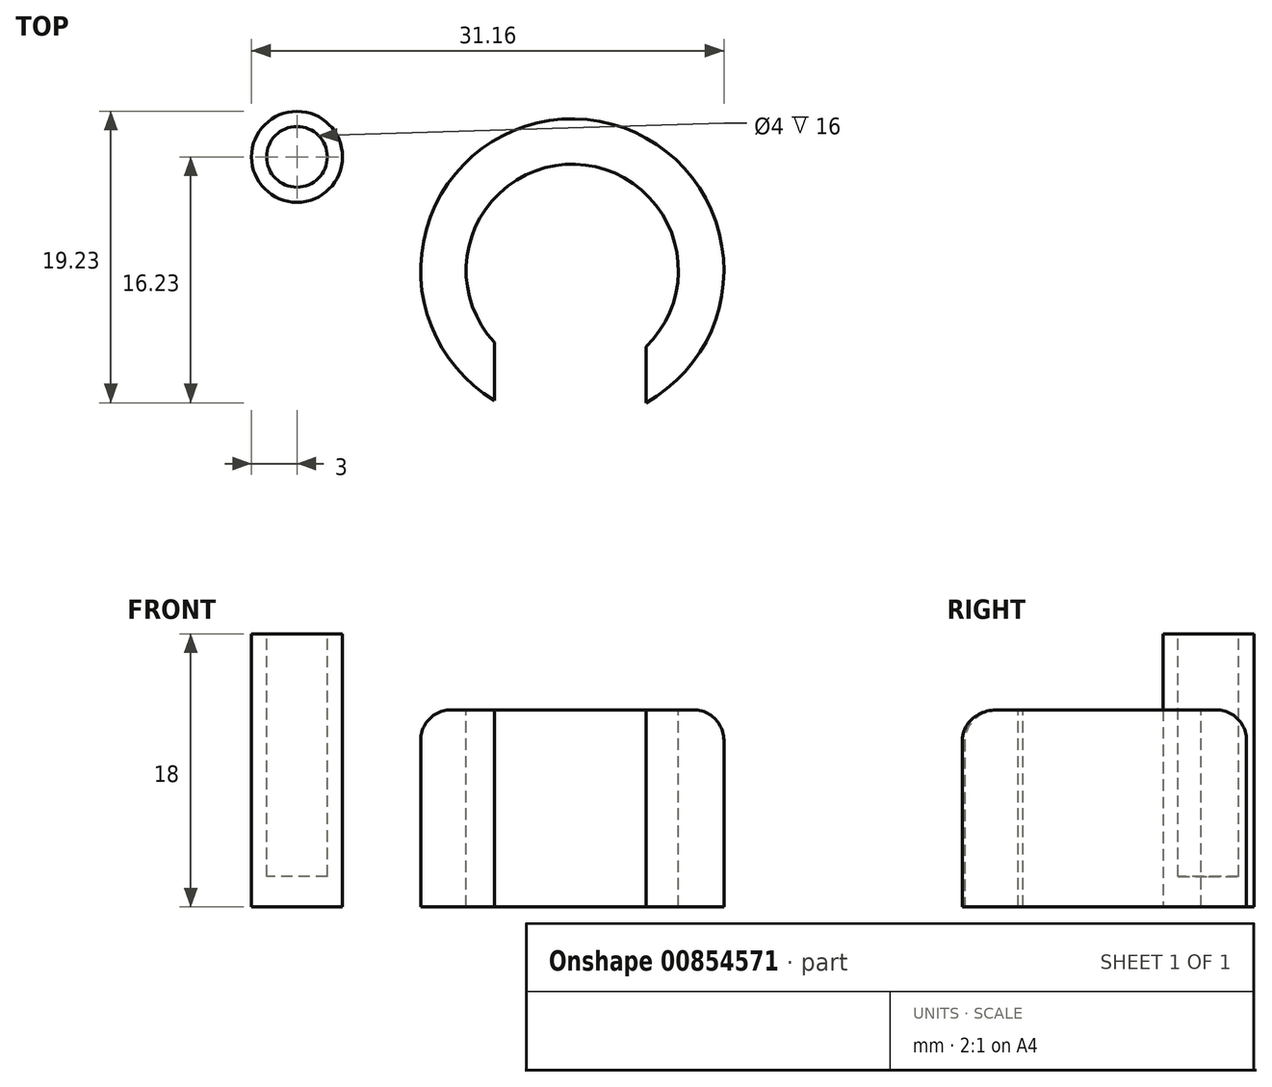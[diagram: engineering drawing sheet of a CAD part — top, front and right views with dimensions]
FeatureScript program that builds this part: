
annotation { "Feature Type Name" : "Feature", "Feature Type Description" : "" }
export const myFeature = defineFeature(function(context is Context, id is Id, definition is map)
    precondition{}
    {
        {
            var Q0;
            Q0=qCreatedBy(makeId("Top.planeOp"),FACE);
            var sketch = newSketch(context, id + "F0", { "sketchPlane" : qUnion([Q0])});
            skCircle(sketch, "E0", {"center": v(0, 0) * mm, "radius": 10 * mm});
            skSolve(sketch);
        }
        {
            var Q0;
            Q0 = qSketchRegion(id + "F0", true);
            extrude(context, id + "F1", {"entities" : qUnion([Q0]), "depth" : 13 * mm, "offsetDistance" : 25 * mm});
        }
        {
            var Q0;
            Q0=makeQuery(id+"F1.opExtrude","CAP_FACE",FACE,{"disambiguationData":[OSD([sQuery(id+"F0.wireOp",EDGE,"E0")])],"isStart":false});
            var sketch = newSketch(context, id + "F2", { "sketchPlane" : qUnion([Q0])});
            skCircle(sketch, "E1", {"center": v(0, 0) * mm, "radius": 7 * mm});
            skSolve(sketch);
        }
        {
            var Q0;
            Q0 = qSketchRegion(id + "F2", true);
            extrude(context, id + "F3", {"entities" : qUnion([Q0]), "operationType" : NewBodyOperationType.REMOVE, "oppositeDirection" : true, "depth" : 13 * mm, "offsetDistance" : 25 * mm});
        }
        {
            var Q0;
            Q0=makeQuery(id+"F1.opExtrude","CAP_FACE",FACE,{"disambiguationData":[OSD([sQuery(id+"F0.wireOp",EDGE,"E0")])],"isStart":false});
            var sketch = newSketch(context, id + "F4", { "sketchPlane" : qUnion([Q0])});
            skPoint(sketch, "E2.middle", {"position": v(0, 0) * mm});
            skLineSegment(sketch, "E3.bottom", {"start": v(-5.14, -2.24) * mm, "end": v(4.86, -2.24) * mm});
            skLineSegment(sketch, "E3.top", {"start": v(-5.14, -15.24) * mm, "end": v(4.86, -15.24) * mm});
            skLineSegment(sketch, "E3.left", {"start": v(-5.14, -2.24) * mm, "end": v(-5.14, -15.24) * mm});
            skLineSegment(sketch, "E3.right", {"start": v(4.86, -2.24) * mm, "end": v(4.86, -15.24) * mm});
            skSolve(sketch);
        }
        {
            var Q0;
            Q0 = qSketchRegion(id + "F4", true);
            extrude(context, id + "F5", {"entities" : qUnion([Q0]), "operationType" : NewBodyOperationType.REMOVE, "oppositeDirection" : true, "depth" : 13 * mm, "offsetDistance" : 25 * mm});
        }
        {
            var Q0;
            Q0=qCreatedBy(makeId("Top.planeOp"),FACE);
            var sketch = newSketch(context, id + "F6", { "sketchPlane" : qUnion([Q0])});
            skCircle(sketch, "E4", {"center": v(-18.16, 7.49) * mm, "radius": 3 * mm});
            skSolve(sketch);
        }
        {
            var Q0;
            Q0 = qSketchRegion(id + "F6", true);
            extrude(context, id + "F7", {"entities" : qUnion([Q0]), "depth" : 18 * mm, "offsetDistance" : 25 * mm});
        }
        {
            var Q0;
            Q0=makeQuery(id+"F7.opExtrude","CAP_FACE",FACE,{"disambiguationData":[OSD([sQuery(id+"F6.wireOp",EDGE,"E4")])],"isStart":false});
            var sketch = newSketch(context, id + "F8", { "sketchPlane" : qUnion([Q0])});
            skCircle(sketch, "E5", {"center": v(-18.16, 7.49) * mm, "radius": 2 * mm});
            skSolve(sketch);
        }
        {
            var Q0;
            Q0 = qSketchRegion(id + "F8", true);
            extrude(context, id + "F9", {"entities" : qUnion([Q0]), "operationType" : NewBodyOperationType.REMOVE, "oppositeDirection" : true, "depth" : 16 * mm, "offsetDistance" : 25 * mm});
        }
        {
            var Q0;
            Q0=makeQuery(id+"F1.opExtrude","CAP_EDGE",EDGE,{"disambiguationData":[OSD([sQuery(id+"F0.wireOp",EDGE,"E0")])],"isStart":false});
            fillet(context, id + "F10", {"entities" : qUnion([Q0]), "radius" : 2 * mm, "tangentPropagation" : true, "allowEdgeOverflow" : false});
        }
    });
